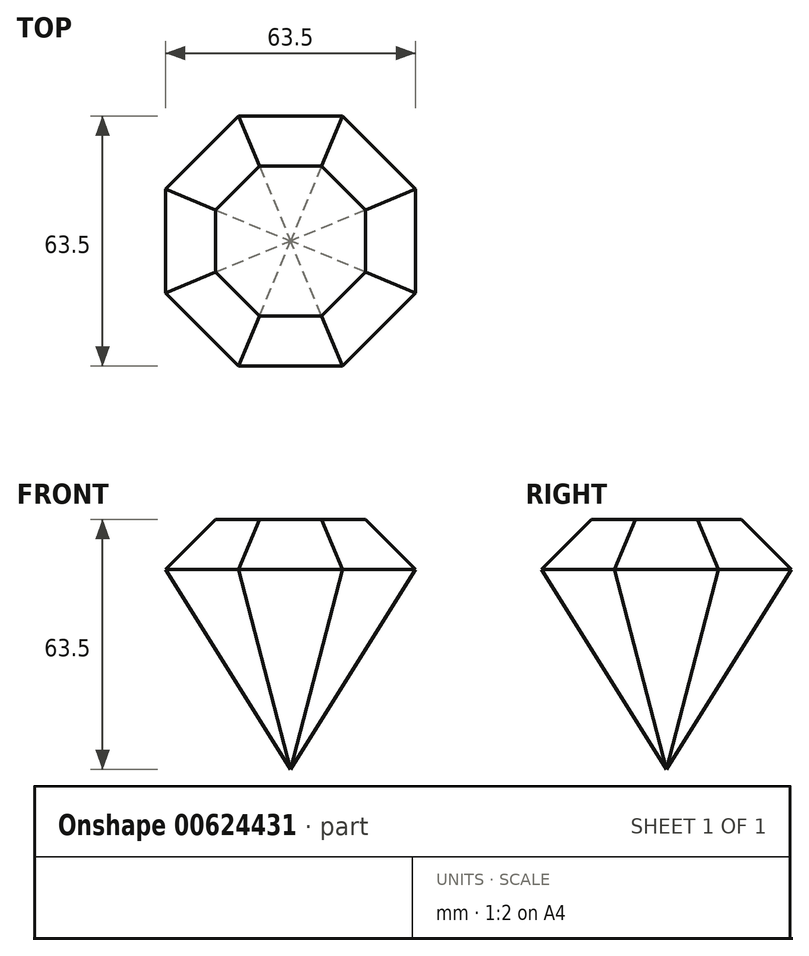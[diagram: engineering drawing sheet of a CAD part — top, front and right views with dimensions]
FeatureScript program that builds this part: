
annotation { "Feature Type Name" : "Feature", "Feature Type Description" : "" }
export const myFeature = defineFeature(function(context is Context, id is Id, definition is map)
    precondition{}
    {
        {
            var Q0;
            Q0=qCreatedBy(makeId("Top.planeOp"),FACE);
            var sketch = newSketch(context, id + "F0", { "sketchPlane" : qUnion([Q0])});
            skCircle(sketch, "E0.cCircle", {"center": v(0, 0) * mm, "radius": 31.75 * mm, "construction": true});
            skLineSegment(sketch, "E0.0", {"start": v(-31.75, -13.15) * mm, "end": v(-31.75, 13.15) * mm});
            skLineSegment(sketch, "E0.1", {"start": v(-31.75, 13.15) * mm, "end": v(-13.15, 31.75) * mm});
            skLineSegment(sketch, "E0.2", {"start": v(-13.15, 31.75) * mm, "end": v(13.15, 31.75) * mm});
            skLineSegment(sketch, "E0.3", {"start": v(13.15, 31.75) * mm, "end": v(31.75, 13.15) * mm});
            skLineSegment(sketch, "E0.4", {"start": v(31.75, 13.15) * mm, "end": v(31.75, -13.15) * mm});
            skLineSegment(sketch, "E0.5", {"start": v(31.75, -13.15) * mm, "end": v(13.15, -31.75) * mm});
            skLineSegment(sketch, "E0.6", {"start": v(13.15, -31.75) * mm, "end": v(-13.15, -31.75) * mm});
            skLineSegment(sketch, "E0.7", {"start": v(-13.15, -31.75) * mm, "end": v(-31.75, -13.15) * mm});
            skPoint(sketch, "E0.0.midPoint", {"position": v(-31.75, 0) * mm});
            skSolve(sketch);
        }
        {
            var Q0;
            Q0=makeQuery(id+"F0.imprint","IMPRINT",FACE,{"disambiguationData":[TD([[makeQuery(id+"F0.imprint","IMPRINT",EDGE,{"derivedFrom":sQuery(id+"F0.wireOp",EDGE,"E0.0")}),-1.0]])]});
            extrude(context, id + "F1", {"entities" : qUnion([Q0]), "depth" : 12.7 * mm, "offsetDistance" : 25.4 * mm});
        }
        {
            var Q0;
            Q0=makeQuery(id+"F1.opExtrude","CAP_FACE",FACE,{"disambiguationData":[OSD([sQuery(id+"F0.wireOp",EDGE,"E0.0"),sQuery(id+"F0.wireOp",EDGE,"E0.1"),sQuery(id+"F0.wireOp",EDGE,"E0.2"),sQuery(id+"F0.wireOp",EDGE,"E0.3"),sQuery(id+"F0.wireOp",EDGE,"E0.4"),sQuery(id+"F0.wireOp",EDGE,"E0.5"),sQuery(id+"F0.wireOp",EDGE,"E0.6"),sQuery(id+"F0.wireOp",EDGE,"E0.7")])],"isStart":false});
            chamfer(context, id + "F2", {"entities" : qUnion([Q0]), "chamferType" : ChamferType.OFFSET_ANGLE, "width" : 12.7 * mm, "oppositeDirection" : false, "angle" : 45 * degree, "tangentPropagation" : true});
        }
        {
            var Q0;
            Q0=makeQuery(id+"F1.opExtrude","CAP_FACE",FACE,{"disambiguationData":[OSD([sQuery(id+"F0.wireOp",EDGE,"E0.0"),sQuery(id+"F0.wireOp",EDGE,"E0.1"),sQuery(id+"F0.wireOp",EDGE,"E0.2"),sQuery(id+"F0.wireOp",EDGE,"E0.3"),sQuery(id+"F0.wireOp",EDGE,"E0.4"),sQuery(id+"F0.wireOp",EDGE,"E0.5"),sQuery(id+"F0.wireOp",EDGE,"E0.6"),sQuery(id+"F0.wireOp",EDGE,"E0.7")])],"isStart":true});
            cPlane(context, id + "F3", {"entities" : qUnion([Q0]), "cplaneType" : CPlaneType.OFFSET, "offset" : 50.8 * mm, "width" : 152.4 * mm, "height" : 152.4 * mm});
        }
        {
            var Q0;
            Q0=qCreatedBy(id+"F3.planeOp",FACE);
            var sketch = newSketch(context, id + "F4", { "sketchPlane" : qUnion([Q0])});
            skPoint(sketch, "E1", {"position": v(0, 0) * mm});
            skSolve(sketch);
        }
        {
            var Q1;
            Q1=makeQuery(id+"F1.opExtrude","CAP_FACE",FACE,{"disambiguationData":[OSD([sQuery(id+"F0.wireOp",EDGE,"E0.0"),sQuery(id+"F0.wireOp",EDGE,"E0.1"),sQuery(id+"F0.wireOp",EDGE,"E0.2"),sQuery(id+"F0.wireOp",EDGE,"E0.3"),sQuery(id+"F0.wireOp",EDGE,"E0.4"),sQuery(id+"F0.wireOp",EDGE,"E0.5"),sQuery(id+"F0.wireOp",EDGE,"E0.6"),sQuery(id+"F0.wireOp",EDGE,"E0.7")])],"isStart":true});
            var Q2;
            Q2=sQuery(id+"F4.wireOp",VERTEX,"E1");
            loft(context, id + "F5", {"operationType" : NewBodyOperationType.ADD, "sheetProfilesArray" : [{ "sheetProfileEntities" : qUnion([Q1]) }, { "sheetProfileEntities" : qUnion([Q2]) }]});
        }
    });
